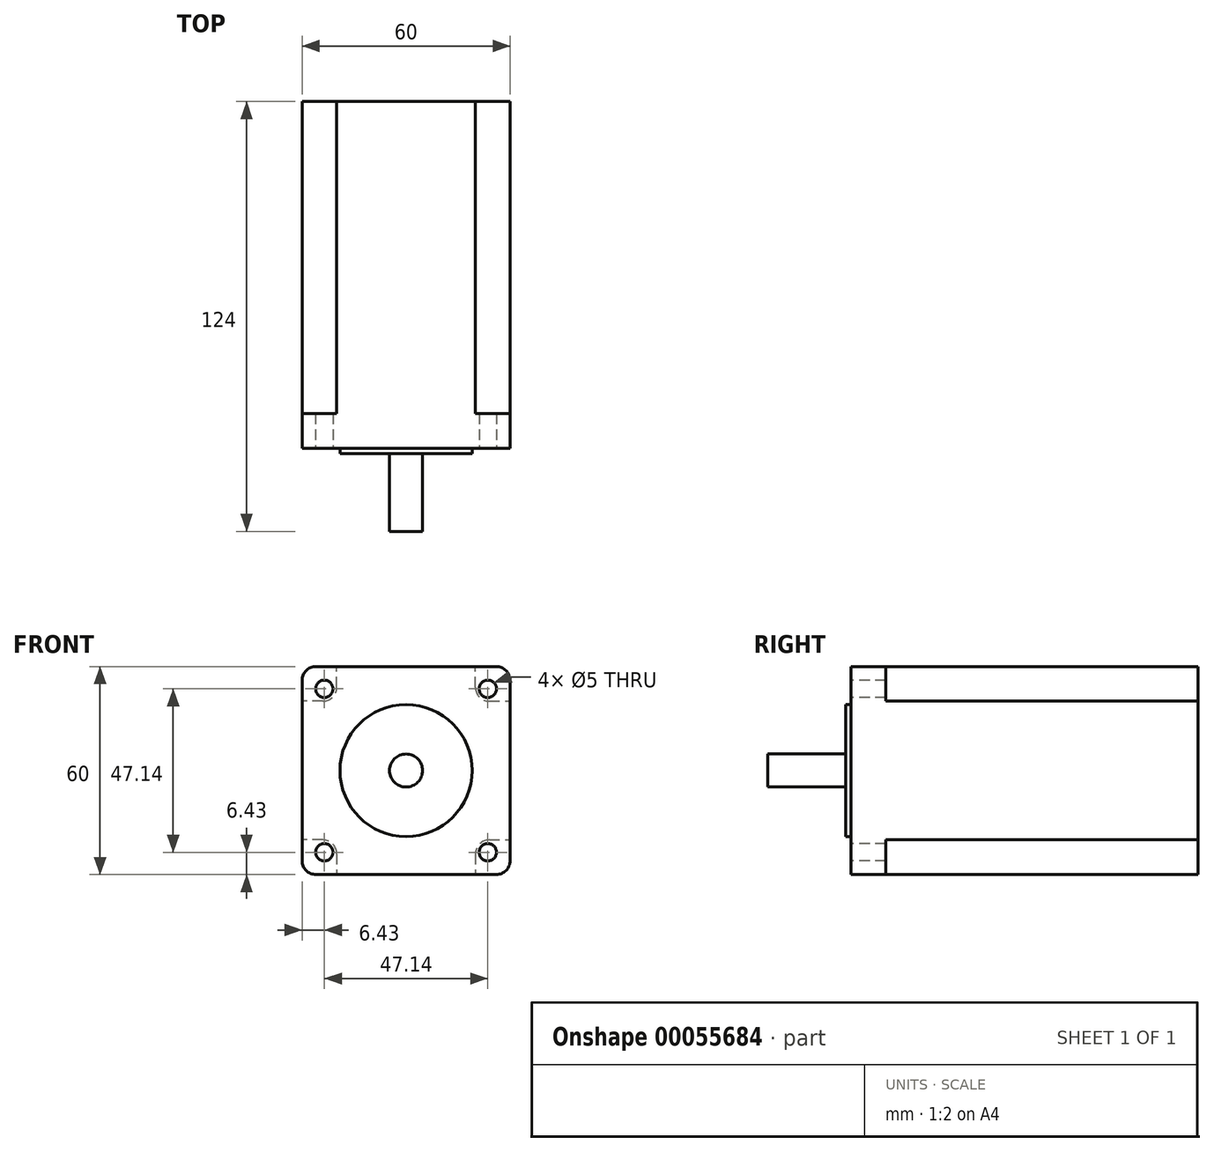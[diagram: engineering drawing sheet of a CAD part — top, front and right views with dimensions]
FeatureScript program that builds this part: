
annotation { "Feature Type Name" : "Feature", "Feature Type Description" : "" }
export const myFeature = defineFeature(function(context is Context, id is Id, definition is map)
    precondition{}
    {
        {
            var Q0;
            Q0=qCreatedBy(makeId("Front.planeOp"),FACE);
            var sketch = newSketch(context, id + "F0", { "sketchPlane" : qUnion([Q0])});
            skLineSegment(sketch, "E0.bottom", {"start": v(4, 0) * mm, "end": v(56, 0) * mm});
            skLineSegment(sketch, "E0.top", {"start": v(4, 60) * mm, "end": v(56, 60) * mm});
            skLineSegment(sketch, "E0.left", {"start": v(0, 4) * mm, "end": v(0, 56) * mm});
            skLineSegment(sketch, "E0.right", {"start": v(60, 4) * mm, "end": v(60, 56) * mm});
            skPoint(sketch, "E1.visualSharp", {"position": v(0, 60) * mm});
            skArc(sketch, "E1.filletArc", {"start": v(4, 60) * mm, "mid": v(1.17, 58.83) * mm, "end": v(0, 56) * mm});
            skPoint(sketch, "E2.visualSharp", {"position": v(60, 60) * mm});
            skArc(sketch, "E2.filletArc", {"start": v(60, 56) * mm, "mid": v(58.83, 58.83) * mm, "end": v(56, 60) * mm});
            skPoint(sketch, "E3.visualSharp", {"position": v(60, 0) * mm});
            skArc(sketch, "E3.filletArc", {"start": v(56, 0) * mm, "mid": v(58.83, 1.17) * mm, "end": v(60, 4) * mm});
            skPoint(sketch, "E4.visualSharp", {"position": v(0, 0) * mm});
            skArc(sketch, "E4.filletArc", {"start": v(0, 4) * mm, "mid": v(1.17, 1.17) * mm, "end": v(4, 0) * mm});
            skSolve(sketch);
        }
        {
            var Q0;
            Q0 = qSketchRegion(id + "F0", true);
            extrude(context, id + "F1", {"entities" : qUnion([Q0]), "oppositeDirection" : true, "depth" : 10 * mm});
        }
        {
            var Q0;
            Q0=makeQuery(id+"F1.opExtrude","CAP_FACE",FACE,{"disambiguationData":[OSD([sQuery(id+"F0.wireOp",EDGE,"E0.bottom"),sQuery(id+"F0.wireOp",EDGE,"E0.top"),sQuery(id+"F0.wireOp",EDGE,"E0.left"),sQuery(id+"F0.wireOp",EDGE,"E0.right"),sQuery(id+"F0.wireOp",EDGE,"E1.filletArc"),sQuery(id+"F0.wireOp",EDGE,"E2.filletArc"),sQuery(id+"F0.wireOp",EDGE,"E3.filletArc"),sQuery(id+"F0.wireOp",EDGE,"E4.filletArc")])],"isStart":true});
            var sketch = newSketch(context, id + "F2", { "sketchPlane" : qUnion([Q0])});
            skLineSegment(sketch, "E5", {"start": v(30, 60) * mm, "end": v(30, 0) * mm});
            skCircle(sketch, "E6", {"center": v(30, 30) * mm, "radius": 19.05 * mm});
            skSolve(sketch);
        }
        {
            var Q0;
            Q0 = qSketchRegion(id + "F2", true);
            extrude(context, id + "F3", {"entities" : qUnion([Q0]), "operationType" : NewBodyOperationType.ADD, "depth" : 1.6 * mm});
        }
        {
            var Q0;
            Q0=makeQuery(id+"F1.opExtrude","CAP_FACE",FACE,{"disambiguationData":[OSD([sQuery(id+"F0.wireOp",EDGE,"E0.bottom"),sQuery(id+"F0.wireOp",EDGE,"E0.top"),sQuery(id+"F0.wireOp",EDGE,"E0.left"),sQuery(id+"F0.wireOp",EDGE,"E0.right"),sQuery(id+"F0.wireOp",EDGE,"E1.filletArc"),sQuery(id+"F0.wireOp",EDGE,"E2.filletArc"),sQuery(id+"F0.wireOp",EDGE,"E3.filletArc"),sQuery(id+"F0.wireOp",EDGE,"E4.filletArc")])],"isStart":true});
            var sketch = newSketch(context, id + "F4", { "sketchPlane" : qUnion([Q0])});
            skLineSegment(sketch, "E7", {"start": v(30, 60) * mm, "end": v(30, 0) * mm});
            skCircle(sketch, "E8", {"center": v(30, 30) * mm, "radius": 4.76 * mm});
            skSolve(sketch);
        }
        {
            var Q0;
            Q0 = qSketchRegion(id + "F4", true);
            extrude(context, id + "F5", {"entities" : qUnion([Q0]), "operationType" : NewBodyOperationType.ADD, "depth" : 24 * mm});
        }
        {
            var Q0;
            Q0=makeQuery(id+"F1.opExtrude","CAP_FACE",FACE,{"disambiguationData":[OSD([sQuery(id+"F0.wireOp",EDGE,"E0.bottom"),sQuery(id+"F0.wireOp",EDGE,"E0.top"),sQuery(id+"F0.wireOp",EDGE,"E0.left"),sQuery(id+"F0.wireOp",EDGE,"E0.right"),sQuery(id+"F0.wireOp",EDGE,"E1.filletArc"),sQuery(id+"F0.wireOp",EDGE,"E2.filletArc"),sQuery(id+"F0.wireOp",EDGE,"E3.filletArc"),sQuery(id+"F0.wireOp",EDGE,"E4.filletArc")])],"isStart":true});
            var sketch = newSketch(context, id + "F6", { "sketchPlane" : qUnion([Q0])});
            skLineSegment(sketch, "E9", {"start": v(30, 60) * mm, "end": v(30, 0) * mm});
            skLineSegment(sketch, "E10", {"start": v(0, 30) * mm, "end": v(60, 30) * mm});
            skPoint(sketch, "E11", {"position": v(6.43, 53.57) * mm});
            skPoint(sketch, "E12", {"position": v(53.57, 53.57) * mm});
            skPoint(sketch, "E13", {"position": v(53.57, 6.43) * mm});
            skPoint(sketch, "E14", {"position": v(6.43, 6.43) * mm});
            skSolve(sketch);
        }
        {
            var Q0;
            Q0=makeQuery(id+"F1.opExtrude","CAP_FACE",FACE,{"disambiguationData":[OSD([sQuery(id+"F0.wireOp",EDGE,"E0.bottom"),sQuery(id+"F0.wireOp",EDGE,"E0.top"),sQuery(id+"F0.wireOp",EDGE,"E0.left"),sQuery(id+"F0.wireOp",EDGE,"E0.right"),sQuery(id+"F0.wireOp",EDGE,"E1.filletArc"),sQuery(id+"F0.wireOp",EDGE,"E2.filletArc"),sQuery(id+"F0.wireOp",EDGE,"E3.filletArc"),sQuery(id+"F0.wireOp",EDGE,"E4.filletArc")])],"isStart":false});
            extrude(context, id + "F7", {"entities" : qUnion([Q0]), "operationType" : NewBodyOperationType.ADD, "depth" : 90 * mm});
        }
        {
            var Q0;
            Q0=makeQuery(id+"F7.opExtrude","CAP_FACE",FACE,{"disambiguationData":[OSD([sQuery(id+"F0.wireOp",EDGE,"E0.bottom"),sQuery(id+"F0.wireOp",EDGE,"E0.top"),sQuery(id+"F0.wireOp",EDGE,"E0.left"),sQuery(id+"F0.wireOp",EDGE,"E0.right"),sQuery(id+"F0.wireOp",EDGE,"E1.filletArc"),sQuery(id+"F0.wireOp",EDGE,"E2.filletArc"),sQuery(id+"F0.wireOp",EDGE,"E3.filletArc"),sQuery(id+"F0.wireOp",EDGE,"E4.filletArc")])],"isStart":false});
            var sketch = newSketch(context, id + "F8", { "sketchPlane" : qUnion([Q0])});
            skLineSegment(sketch, "E15.bottom", {"start": v(-54, 50) * mm, "end": v(-60, 50) * mm});
            skLineSegment(sketch, "E15.top", {"start": v(-50, 60) * mm, "end": v(-60, 60) * mm});
            skLineSegment(sketch, "E15.left", {"start": v(-50, 54) * mm, "end": v(-50, 60) * mm});
            skLineSegment(sketch, "E15.right", {"start": v(-60, 50) * mm, "end": v(-60, 60) * mm});
            skLineSegment(sketch, "E16.bottom", {"start": v(-6, 50) * mm, "end": v(0, 50) * mm});
            skLineSegment(sketch, "E16.top", {"start": v(-10, 60) * mm, "end": v(0, 60) * mm});
            skLineSegment(sketch, "E16.left", {"start": v(-10, 54) * mm, "end": v(-10, 60) * mm});
            skLineSegment(sketch, "E16.right", {"start": v(0, 50) * mm, "end": v(0, 60) * mm});
            skLineSegment(sketch, "E17.bottom", {"start": v(-54, 10) * mm, "end": v(-60, 10) * mm});
            skLineSegment(sketch, "E17.top", {"start": v(-50, 0) * mm, "end": v(-60, 0) * mm});
            skLineSegment(sketch, "E17.left", {"start": v(-50, 6) * mm, "end": v(-50, 0) * mm});
            skLineSegment(sketch, "E17.right", {"start": v(-60, 10) * mm, "end": v(-60, 0) * mm});
            skLineSegment(sketch, "E18.bottom", {"start": v(-6, 10) * mm, "end": v(0, 10) * mm});
            skLineSegment(sketch, "E18.top", {"start": v(-10, 0) * mm, "end": v(0, 0) * mm});
            skLineSegment(sketch, "E18.left", {"start": v(-10, 6) * mm, "end": v(-10, 0) * mm});
            skLineSegment(sketch, "E18.right", {"start": v(0, 10) * mm, "end": v(0, 0) * mm});
            skPoint(sketch, "E19.visualSharp", {"position": v(-50, 50) * mm});
            skArc(sketch, "E19.filletArc", {"start": v(-54, 50) * mm, "mid": v(-51.17, 51.17) * mm, "end": v(-50, 54) * mm});
            skPoint(sketch, "E20.visualSharp", {"position": v(-10, 50) * mm});
            skArc(sketch, "E20.filletArc", {"start": v(-10, 54) * mm, "mid": v(-8.83, 51.17) * mm, "end": v(-6, 50) * mm});
            skPoint(sketch, "E21.visualSharp", {"position": v(-10, 10) * mm});
            skArc(sketch, "E21.filletArc", {"start": v(-6, 10) * mm, "mid": v(-8.83, 8.83) * mm, "end": v(-10, 6) * mm});
            skPoint(sketch, "E22.visualSharp", {"position": v(-50, 10) * mm});
            skArc(sketch, "E22.filletArc", {"start": v(-50, 6) * mm, "mid": v(-51.17, 8.83) * mm, "end": v(-54, 10) * mm});
            skSolve(sketch);
        }
        {
            var Q0;
            Q0 = qSketchRegion(id + "F8", true);
            extrude(context, id + "F9", {"entities" : qUnion([Q0]), "operationType" : NewBodyOperationType.REMOVE, "oppositeDirection" : true, "depth" : 90 * mm});
        }
        {
            var Q0;
            Q0=sQuery(id+"F6.wireOp",VERTEX,"E11");
            var Q1;
            Q1=sQuery(id+"F6.wireOp",VERTEX,"E12");
            var Q2;
            Q2=sQuery(id+"F6.wireOp",VERTEX,"E13");
            var Q3;
            Q3=sQuery(id+"F6.wireOp",VERTEX,"E14");
            var Q4;
            Q4=makeQuery(id+"F1.opExtrude","SWEPT_BODY",BODY,{"disambiguationData":[OSD([sQuery(id+"F0.wireOp",EDGE,"E0.bottom"),sQuery(id+"F0.wireOp",EDGE,"E0.top"),sQuery(id+"F0.wireOp",EDGE,"E0.left"),sQuery(id+"F0.wireOp",EDGE,"E0.right"),sQuery(id+"F0.wireOp",EDGE,"E1.filletArc"),sQuery(id+"F0.wireOp",EDGE,"E2.filletArc"),sQuery(id+"F0.wireOp",EDGE,"E3.filletArc"),sQuery(id+"F0.wireOp",EDGE,"E4.filletArc")])]});
            hole(context, id + "F10", {"style" : HoleStyle.SIMPLE, "holeDiameter" : 5 * mm, "endStyle" : HoleEndStyle.THROUGH, "locations" : qUnion([Q0, Q1, Q2, Q3]), "scope" : qUnion([Q4])});
        }
    });
